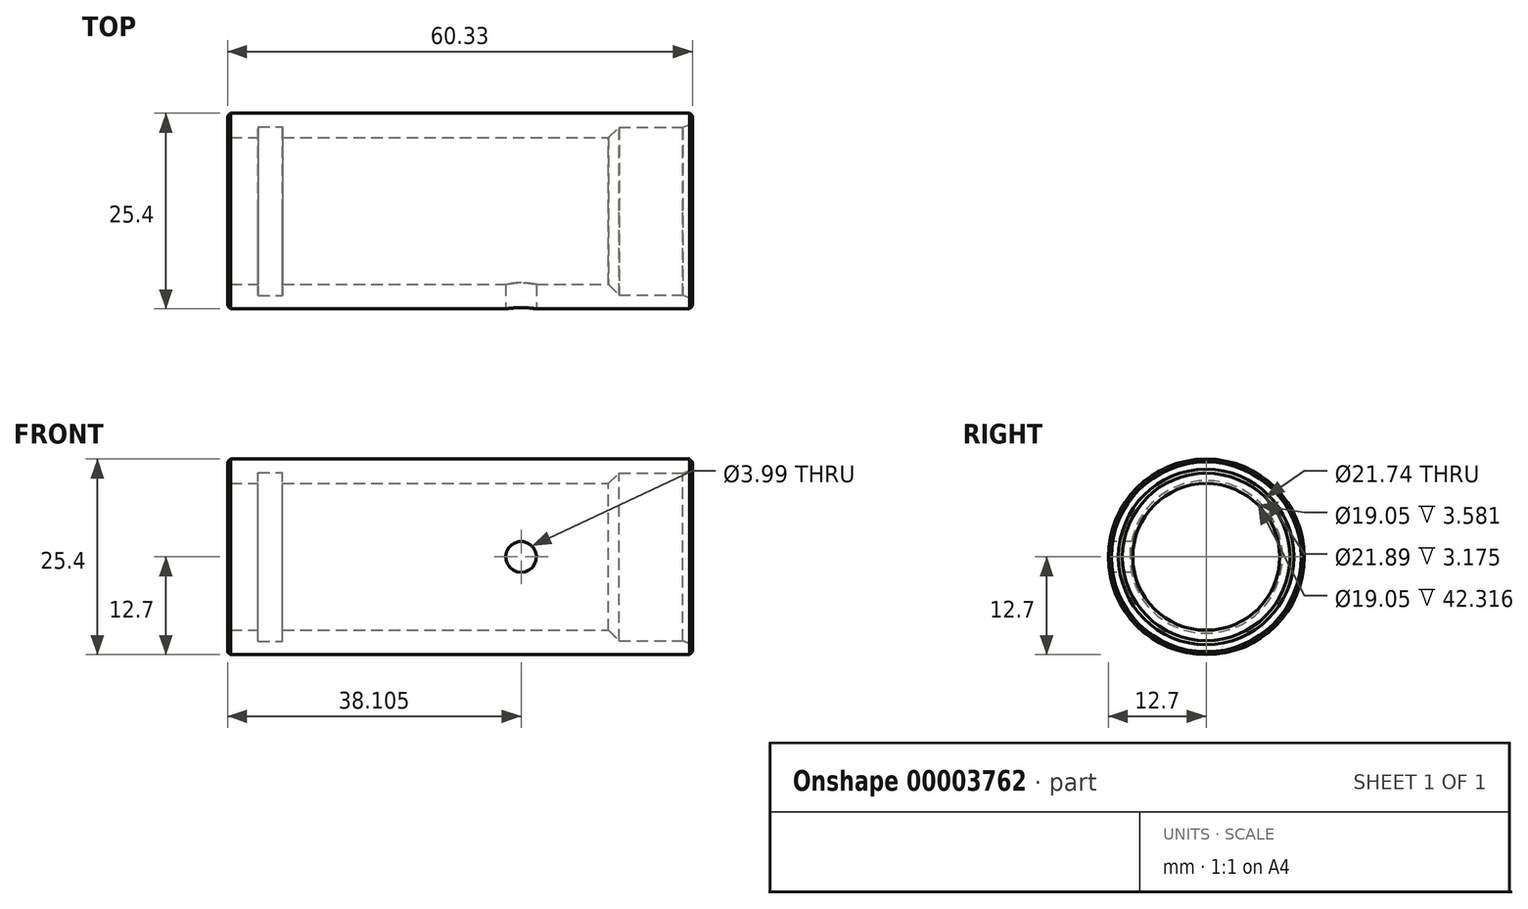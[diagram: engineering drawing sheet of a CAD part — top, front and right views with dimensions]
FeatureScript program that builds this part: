
annotation { "Feature Type Name" : "Feature", "Feature Type Description" : "" }
export const myFeature = defineFeature(function(context is Context, id is Id, definition is map)
    precondition{}
    {
        {
            var Q0;
            Q0=qCreatedBy(makeId("Front.planeOp"),FACE);
            var sketch = newSketch(context, id + "F0", { "sketchPlane" : qUnion([Q0])});
            skLineSegment(sketch, "E0", {"start": v(-1.23, 10.87) * mm, "end": v(-9.52, 10.87) * mm});
            skLineSegment(sketch, "E1", {"start": v(-9.52, 10.87) * mm, "end": v(-10.87, 9.52) * mm});
            skLineSegment(sketch, "E2", {"start": v(-10.87, 9.52) * mm, "end": v(-53.19, 9.52) * mm});
            skLineSegment(sketch, "E3", {"start": v(-53.19, 9.52) * mm, "end": v(-53.19, 10.95) * mm});
            skLineSegment(sketch, "E4", {"start": v(-53.19, 10.95) * mm, "end": v(-56.36, 10.95) * mm});
            skLineSegment(sketch, "E5", {"start": v(-56.36, 10.95) * mm, "end": v(-56.36, 9.52) * mm});
            skLineSegment(sketch, "E6", {"start": v(-56.36, 9.52) * mm, "end": v(-60.33, 9.52) * mm});
            skLineSegment(sketch, "E7", {"start": v(-60.33, 9.52) * mm, "end": v(-60.33, 12.7) * mm});
            skLineSegment(sketch, "E8", {"start": v(-60.33, 12.7) * mm, "end": v(0, 12.7) * mm});
            skLineSegment(sketch, "E9", {"start": v(0, 12.7) * mm, "end": v(0, 11.38) * mm});
            skLineSegment(sketch, "E10", {"start": v(0, 11.38) * mm, "end": v(-1.23, 10.87) * mm});
            skLineSegment(sketch, "E11", {"start": v(0, 0) * mm, "end": v(-79.5, 0) * mm, "construction": true});
            skSolve(sketch);
        }
        {
            var Q0;
            Q0=makeQuery(id+"F0.imprint","IMPRINT",FACE,{"disambiguationData":[TD([[makeQuery(id+"F0.imprint","IMPRINT",EDGE,{"derivedFrom":sQuery(id+"F0.wireOp",EDGE,"E0")}),-1.0]])]});
            var Q1;
            Q1=sQuery(id+"F0.wireOp",EDGE,"E11");
            revolve(context, id + "F1", {"entities" : qUnion([Q0]), "axis" : qUnion([Q1]), "revolveType" : RevolveType.FULL});
        }
        {
            var Q0;
            Q0=qCreatedBy(makeId("Front.planeOp"),FACE);
            cPlane(context, id + "F2", {"entities" : qUnion([Q0]), "cplaneType" : CPlaneType.OFFSET, "offset" : 12.7 * mm, "width" : 152.4 * mm, "height" : 152.4 * mm});
        }
        {
            var Q0;
            Q0=qCreatedBy(id+"F2.planeOp",FACE);
            var sketch = newSketch(context, id + "F3", { "sketchPlane" : qUnion([Q0])});
            skCircle(sketch, "E12", {"center": v(-22.23, 0) * mm, "radius": 2 * mm});
            skSolve(sketch);
        }
        {
            var Q0;
            Q0 = qSketchRegion(id + "F3", true);
            extrude(context, id + "F4", {"entities" : qUnion([Q0]), "operationType" : NewBodyOperationType.REMOVE, "endBound" : BoundingType.UP_TO_NEXT, "oppositeDirection" : true, "depth" : 25.4 * mm});
        }
        {
            var Q0;
            Q0=makeQuery(id+"F1.opRevolve","SWEPT_EDGE",EDGE,{"disambiguationData":[OSD([sQuery(id+"F0.wireOp",EDGE,"E8"),sQuery(id+"F0.wireOp",EDGE,"E9")])]});
            var Q1;
            Q1=makeQuery(id+"F1.opRevolve","SWEPT_FACE",FACE,{"disambiguationData":[OSD([sQuery(id+"F0.wireOp",EDGE,"E7")])]});
            chamfer(context, id + "F5", {"entities" : qUnion([Q0, Q1]), "width" : 0.38 * mm, "tangentPropagation" : true});
        }
    });
